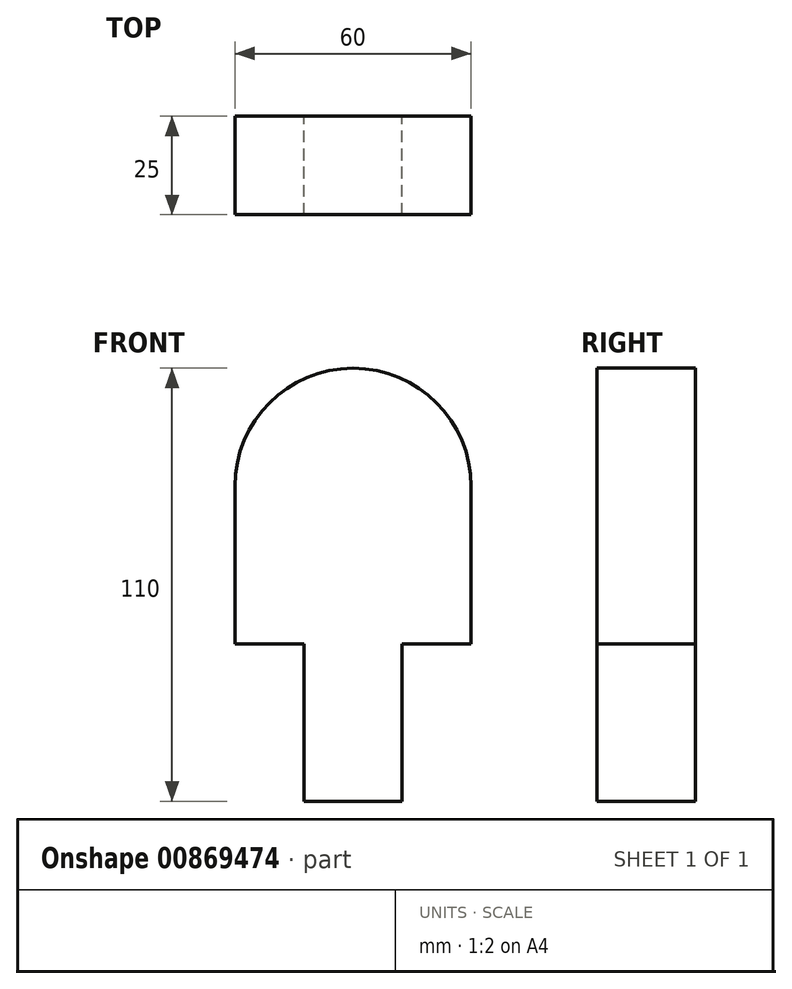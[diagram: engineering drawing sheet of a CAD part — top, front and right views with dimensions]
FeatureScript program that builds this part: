
annotation { "Feature Type Name" : "Feature", "Feature Type Description" : "" }
export const myFeature = defineFeature(function(context is Context, id is Id, definition is map)
    precondition{}
    {
        {
            var Q0;
            Q0=qCreatedBy(makeId("Front.planeOp"),FACE);
            var sketch = newSketch(context, id + "F0", { "sketchPlane" : qUnion([Q0])});
            skLineSegment(sketch, "E0.bottom", {"start": v(-29.06, 17.62) * mm, "end": v(30.94, 17.62) * mm});
            skLineSegment(sketch, "E0.top", {"start": v(-29.06, -22.38) * mm, "end": v(30.94, -22.38) * mm});
            skLineSegment(sketch, "E0.left", {"start": v(-29.06, 17.62) * mm, "end": v(-29.06, -22.38) * mm});
            skLineSegment(sketch, "E0.right", {"start": v(30.94, 17.62) * mm, "end": v(30.94, -22.38) * mm});
            skLineSegment(sketch, "E1", {"start": v(-11.56, -22.38) * mm, "end": v(-11.56, -62.38) * mm});
            skLineSegment(sketch, "E2", {"start": v(13.44, -22.38) * mm, "end": v(13.44, -62.38) * mm});
            skLineSegment(sketch, "E3", {"start": v(13.44, -62.38) * mm, "end": v(-11.56, -62.38) * mm});
            skArc(sketch, "E4", {"start": v(30.94, 17.62) * mm, "mid": v(0.94, 47.62) * mm, "end": v(-29.06, 17.62) * mm});
            skSolve(sketch);
        }
        {
            var Q0;
            Q0=makeQuery(id+"F0.imprint","IMPRINT",FACE,{"disambiguationData":[TD([[makeQuery(id+"F0.imprint","IMPRINT",EDGE,{"derivedFrom":sQuery(id+"F0.wireOp",EDGE,"E0.bottom")}),1.0]])]});
            var Q1;
            Q1=makeQuery(id+"F0.imprint","IMPRINT",FACE,{"disambiguationData":[TD([[makeQuery(id+"F0.imprint","IMPRINT",EDGE,{"derivedFrom":sQuery(id+"F0.wireOp",EDGE,"E0.bottom")}),-1.0]])]});
            var Q2;
            {var subQ0=sQuery(id+"F0.wireOp",EDGE,"E1");Q2=makeQuery(id+"F0.imprint","IMPRINT",FACE,{"disambiguationData":[TD([[makeQuery(id+"F0.imprint","IMPRINT",EDGE,{"derivedFrom":subQ0}),1.0]])]});}
            extrude(context, id + "F1", {"entities" : qUnion([Q0, Q1, Q2]), "endBound" : BoundingType.SYMMETRIC, "depth" : 25 * mm, "offsetDistance" : 25 * mm});
        }
    });
